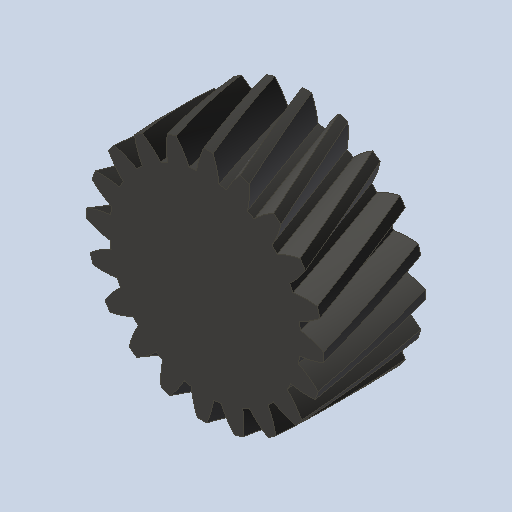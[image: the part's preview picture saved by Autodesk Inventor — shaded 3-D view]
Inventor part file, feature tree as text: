
AUTODESK INVENTOR PART (.ipt)
format: ipt  version: 2023 (Build 270158000, 158)  size: 380,416 bytes
history: native  units: mm (DEFAULTED — no unit token found)
features: plane x3, other x3, sketch x2, extrude x1
ambient origin geometry x8: Origin, YZ Plane, XZ Plane, XY Plane, X Axis, Y Axis, Z Axis, Center Point
bodies: Solid1 (feature_tree)
feature tree (9):
  extrude  "Extrusion1"  Depth=15.0mm TaperAngle=0.0deg
  plane  "Work Plane2"
  plane  "Work Plane8"
  plane  "Work Plane9"
  other  "Spur Gear"
  sketch  "Sketch1"  dims[d0=34.921665mm d1=15.0mm d2=0.0mm]
  sketch  "Sketch2"  dims[d3=31.925333mm d4=10.0mm d5=0.0mm d16=2.25mm d17=0.0mm d34=1.570796mm d39=0.0mm d41=0.0mm d43=2.25mm d46=2.25mm d47=0.0mm d48=0.0mm]
  other  "Srf1"
  other  "Pitch Diameter"
